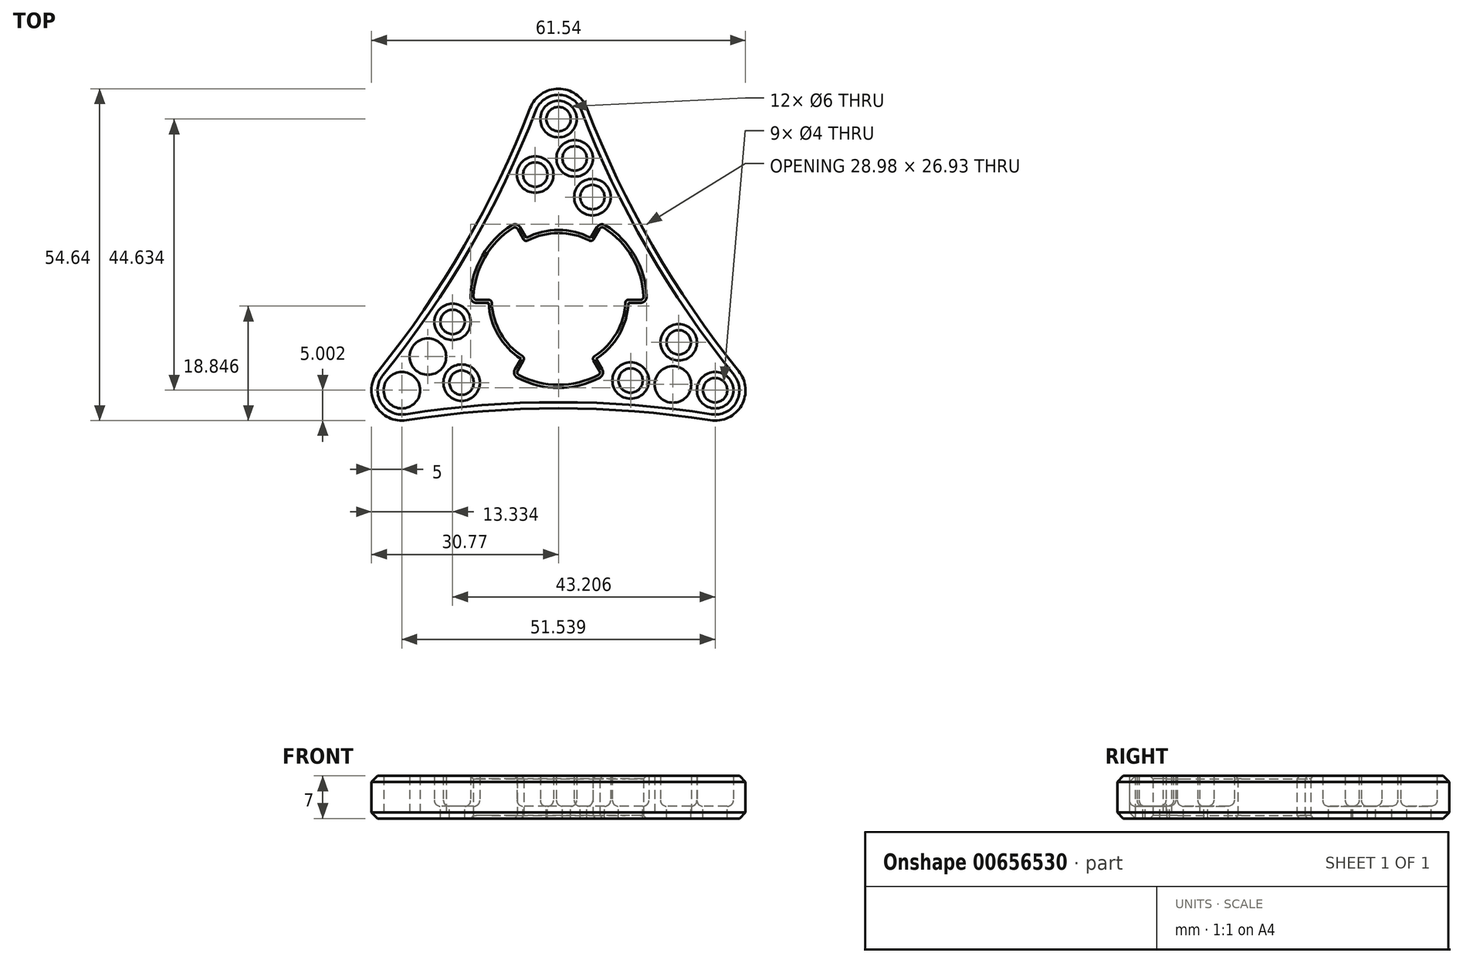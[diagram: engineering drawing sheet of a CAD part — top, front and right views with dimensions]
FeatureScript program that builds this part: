
annotation { "Feature Type Name" : "Feature", "Feature Type Description" : "" }
export const myFeature = defineFeature(function(context is Context, id is Id, definition is map)
    precondition{}
    {
        {
            var Q0;
            Q0=qCreatedBy(makeId("Top.planeOp"),FACE);
            var sketch = newSketch(context, id + "F0", { "sketchPlane" : qUnion([Q0])});
            skCircle(sketch, "E0", {"center": v(0, 0) * mm, "radius": 11 * mm});
            skCircle(sketch, "E1", {"center": v(0, 29.76) * mm, "radius": 3 * mm});
            skCircle(sketch, "E2", {"center": v(-3.83, 20.63) * mm, "radius": 3 * mm});
            skCircle(sketch, "E3", {"center": v(2.65, 23.28) * mm, "radius": 3 * mm});
            skLineSegment(sketch, "E4", {"start": v(0, 0) * mm, "end": v(0, 29.76) * mm, "construction": true});
            skLineSegment(sketch, "E5", {"start": v(0, 45.58) * mm, "end": v(39.48, -22.8) * mm, "construction": true});
            skLineSegment(sketch, "E6", {"start": v(39.48, -22.8) * mm, "end": v(-39.48, -22.8) * mm, "construction": true});
            skLineSegment(sketch, "E7", {"start": v(-39.48, -22.8) * mm, "end": v(0, 45.58) * mm, "construction": true});
            skLineSegment(sketch, "E8", {"start": v(0, 0) * mm, "end": v(-39.48, -22.8) * mm, "construction": true});
            skCircle(sketch, "E9", {"center": v(0, 0) * mm, "radius": 14 * mm});
            skLineSegment(sketch, "E10", {"start": v(-7, 12.12) * mm, "end": v(-5.5, 9.53) * mm});
            skLineSegment(sketch, "E11", {"start": v(-14, 0) * mm, "end": v(-11, 0) * mm});
            skArc(sketch, "E12", {"start": v(0, 45.58) * mm, "mid": v(15.47, 8.93) * mm, "end": v(39.48, -22.8) * mm});
            skArc(sketch, "E13", {"start": v(-39.48, -22.8) * mm, "mid": v(-15.47, 8.93) * mm, "end": v(0, 45.58) * mm});
            skArc(sketch, "E14", {"start": v(39.48, -22.8) * mm, "mid": v(0, -17.86) * mm, "end": v(-39.48, -22.8) * mm});
            skCircle(sketch, "E15", {"center": v(5.57, 16.92) * mm, "radius": 3 * mm});
            skLineSegment(sketch, "E16", {"start": v(-3.83, 20.63) * mm, "end": v(2.65, 23.28) * mm, "construction": true});
            skLineSegment(sketch, "E17", {"start": v(0, 29.76) * mm, "end": v(2.65, 23.28) * mm, "construction": true});
            skCircle(sketch, "E18.1.0", {"center": v(-25.77, -14.88) * mm, "radius": 3 * mm});
            skCircle(sketch, "E18.1.1", {"center": v(-21.48, -9.34) * mm, "radius": 3 * mm});
            skCircle(sketch, "E18.1.2", {"center": v(-17.44, -3.63) * mm, "radius": 3 * mm});
            skCircle(sketch, "E18.1.3", {"center": v(-15.95, -13.63) * mm, "radius": 3 * mm});
            skLineSegment(sketch, "E18.1.4", {"start": v(-7, -12.12) * mm, "end": v(-5.5, -9.53) * mm});
            skLineSegment(sketch, "E18.1.5", {"start": v(7, -12.12) * mm, "end": v(5.5, -9.53) * mm});
            skCircle(sketch, "E18.2.0", {"center": v(25.77, -14.88) * mm, "radius": 3 * mm});
            skCircle(sketch, "E18.2.1", {"center": v(18.83, -13.93) * mm, "radius": 3 * mm});
            skCircle(sketch, "E18.2.2", {"center": v(11.86, -13.28) * mm, "radius": 3 * mm});
            skCircle(sketch, "E18.2.3", {"center": v(19.78, -7) * mm, "radius": 3 * mm});
            skLineSegment(sketch, "E18.2.4", {"start": v(14, 0) * mm, "end": v(11, 0) * mm});
            skLineSegment(sketch, "E18.2.5", {"start": v(7, 12.12) * mm, "end": v(5.5, 9.53) * mm});
            skSolve(sketch);
        }
        {
            var Q0;
            Q0=makeQuery(id+"F0.imprint","IMPRINT",FACE,{"disambiguationData":[TD([[makeQuery(id+"F0.imprint","IMPRINT",EDGE,{"derivedFrom":sQuery(id+"F0.wireOp",EDGE,"E1")}),-1.0]])]});
            var Q1;
            {var subQ0=sQuery(id+"F0.wireOp",EDGE,"E10");Q1=makeQuery(id+"F0.imprint","IMPRINT",FACE,{"disambiguationData":[TD([[makeQuery(id+"F0.imprint","IMPRINT",EDGE,{"derivedFrom":subQ0}),1.0]])]});}
            var Q2;
            {var subQ0=sQuery(id+"F0.wireOp",EDGE,"E11");Q2=makeQuery(id+"F0.imprint","IMPRINT",FACE,{"disambiguationData":[TD([[makeQuery(id+"F0.imprint","IMPRINT",EDGE,{"derivedFrom":subQ0}),-1.0]])]});}
            var Q3;
            {var subQ0=sQuery(id+"F0.wireOp",EDGE,"f7c1c19d-2732-4989-aeff-ee9fb130af58.1.6");Q3=makeQuery(id+"F0.imprint","IMPRINT",FACE,{"disambiguationData":[TD([[makeQuery(id+"F0.imprint","IMPRINT",EDGE,{"derivedFrom":subQ0}),-1.0]])]});}
            var Q4;
            {var subQ0=sQuery(id+"F0.wireOp",EDGE,"E18.1.5");Q4=makeQuery(id+"F0.imprint","IMPRINT",FACE,{"disambiguationData":[TD([[makeQuery(id+"F0.imprint","IMPRINT",EDGE,{"derivedFrom":subQ0}),-1.0]])]});}
            extrude(context, id + "F1", {"entities" : qUnion([Q0, Q1, Q2, Q3, Q4]), "depth" : 7 * mm, "offsetDistance" : 25 * mm});
        }
        {
            var Q0;
            Q0=makeQuery(id+"F1.opExtrude","SWEPT_EDGE",EDGE,{"disambiguationData":[OSD([sQuery(id+"F0.wireOp",EDGE,"E12"),sQuery(id+"F0.wireOp",EDGE,"E14")])]});
            var Q1;
            Q1=makeQuery(id+"F1.opExtrude","SWEPT_EDGE",EDGE,{"disambiguationData":[OSD([sQuery(id+"F0.wireOp",EDGE,"E13"),sQuery(id+"F0.wireOp",EDGE,"E14")])]});
            var Q2;
            Q2=makeQuery(id+"F1.opExtrude","SWEPT_EDGE",EDGE,{"disambiguationData":[OSD([sQuery(id+"F0.wireOp",EDGE,"E12"),sQuery(id+"F0.wireOp",EDGE,"E13")])]});
            fillet(context, id + "F2", {"entities" : qUnion([Q0, Q1, Q2]), "radius" : 5 * mm, "tangentPropagation" : true, "allowEdgeOverflow" : false});
        }
        {
            var Q0;
            Q0=makeQuery(id+"F1.opExtrude","SWEPT_EDGE",EDGE,{"disambiguationData":[OSD([sQuery(id+"F0.wireOp",EDGE,"E9"),sQuery(id+"F0.wireOp",EDGE,"E10")])]});
            var Q1;
            Q1=makeQuery(id+"F1.opExtrude","SWEPT_EDGE",EDGE,{"disambiguationData":[OSD([sQuery(id+"F0.wireOp",EDGE,"E0"),sQuery(id+"F0.wireOp",EDGE,"E10")])]});
            var Q2;
            Q2=makeQuery(id+"F1.opExtrude","SWEPT_EDGE",EDGE,{"disambiguationData":[OSD([sQuery(id+"F0.wireOp",EDGE,"E0"),sQuery(id+"F0.wireOp",EDGE,"E18.2.5")])]});
            var Q3;
            Q3=makeQuery(id+"F1.opExtrude","SWEPT_EDGE",EDGE,{"disambiguationData":[OSD([sQuery(id+"F0.wireOp",EDGE,"E9"),sQuery(id+"F0.wireOp",EDGE,"E18.2.5")])]});
            var Q4;
            Q4=makeQuery(id+"F1.opExtrude","SWEPT_EDGE",EDGE,{"disambiguationData":[OSD([sQuery(id+"F0.wireOp",EDGE,"E9"),sQuery(id+"F0.wireOp",EDGE,"E18.2.4")])]});
            var Q5;
            Q5=makeQuery(id+"F1.opExtrude","SWEPT_EDGE",EDGE,{"disambiguationData":[OSD([sQuery(id+"F0.wireOp",EDGE,"E0"),sQuery(id+"F0.wireOp",EDGE,"E18.2.4")])]});
            var Q6;
            Q6=makeQuery(id+"F1.opExtrude","SWEPT_EDGE",EDGE,{"disambiguationData":[OSD([sQuery(id+"F0.wireOp",EDGE,"E0"),sQuery(id+"F0.wireOp",EDGE,"E18.1.5")])]});
            var Q7;
            Q7=makeQuery(id+"F1.opExtrude","SWEPT_EDGE",EDGE,{"disambiguationData":[OSD([sQuery(id+"F0.wireOp",EDGE,"E9"),sQuery(id+"F0.wireOp",EDGE,"E18.1.5")])]});
            var Q8;
            Q8=makeQuery(id+"F1.opExtrude","SWEPT_EDGE",EDGE,{"disambiguationData":[OSD([sQuery(id+"F0.wireOp",EDGE,"E9"),sQuery(id+"F0.wireOp",EDGE,"E11")])]});
            var Q9;
            Q9=makeQuery(id+"F1.opExtrude","SWEPT_EDGE",EDGE,{"disambiguationData":[OSD([sQuery(id+"F0.wireOp",EDGE,"E0"),sQuery(id+"F0.wireOp",EDGE,"E11")])]});
            var Q10;
            Q10=makeQuery(id+"F1.opExtrude","SWEPT_EDGE",EDGE,{"disambiguationData":[OSD([sQuery(id+"F0.wireOp",EDGE,"E9"),sQuery(id+"F0.wireOp",EDGE,"E18.1.4")])]});
            var Q11;
            Q11=makeQuery(id+"F1.opExtrude","SWEPT_EDGE",EDGE,{"disambiguationData":[OSD([sQuery(id+"F0.wireOp",EDGE,"E0"),sQuery(id+"F0.wireOp",EDGE,"E18.1.4")])]});
            fillet(context, id + "F3", {"entities" : qUnion([Q0, Q1, Q2, Q3, Q4, Q5, Q6, Q7, Q8, Q9, Q10, Q11]), "radius" : 0.5 * mm, "tangentPropagation" : true, "allowEdgeOverflow" : false});
        }
        {
            var Q0;
            {var subQ0=sQuery(id+"F0.wireOp",EDGE,"E0");Q0=makeQuery(id+"F1.opExtrude","CAP_EDGE",EDGE,{"disambiguationData":[OSD([subQ0]),TDD([makeQuery(id+"F0.imprint","IMPRINT",EDGE,{"disambiguationData":[TD([[makeQuery(id+"F0.imprint","INTERSECT",VERTEX,{"derivedFrom":[subQ0,sQuery(id+"F0.wireOp",EDGE,"E18.1.5")]}),-1.0]])],"derivedFrom":subQ0})])],"isStart":true});}
            var Q1;
            {var subQ0=sQuery(id+"F0.wireOp",EDGE,"E0");Q1=makeQuery(id+"F1.opExtrude","CAP_EDGE",EDGE,{"disambiguationData":[OSD([subQ0]),TDD([makeQuery(id+"F0.imprint","IMPRINT",EDGE,{"disambiguationData":[TD([[makeQuery(id+"F0.imprint","INTERSECT",VERTEX,{"derivedFrom":[subQ0,sQuery(id+"F0.wireOp",EDGE,"E18.1.5")]}),-1.0]])],"derivedFrom":subQ0})])],"isStart":false});}
            chamfer(context, id + "F4", {"entities" : qUnion([Q0, Q1]), "width" : 0.5 * mm, "tangentPropagation" : true});
        }
        {
            var Q0;
            Q0=makeQuery(id+"F0.imprint","IMPRINT",FACE,{"disambiguationData":[TD([[makeQuery(id+"F0.imprint","IMPRINT",EDGE,{"derivedFrom":sQuery(id+"F0.wireOp",EDGE,"E1")}),1.0]])]});
            var Q1;
            Q1=makeQuery(id+"F0.imprint","IMPRINT",FACE,{"disambiguationData":[TD([[makeQuery(id+"F0.imprint","IMPRINT",EDGE,{"derivedFrom":sQuery(id+"F0.wireOp",EDGE,"E3")}),1.0]])]});
            var Q2;
            Q2=makeQuery(id+"F0.imprint","IMPRINT",FACE,{"disambiguationData":[TD([[makeQuery(id+"F0.imprint","IMPRINT",EDGE,{"derivedFrom":sQuery(id+"F0.wireOp",EDGE,"E15")}),1.0]])]});
            var Q3;
            Q3=makeQuery(id+"F0.imprint","IMPRINT",FACE,{"disambiguationData":[TD([[makeQuery(id+"F0.imprint","IMPRINT",EDGE,{"derivedFrom":sQuery(id+"F0.wireOp",EDGE,"E2")}),1.0]])]});
            var Q4;
            Q4=makeQuery(id+"F0.imprint","IMPRINT",FACE,{"disambiguationData":[TD([[makeQuery(id+"F0.imprint","IMPRINT",EDGE,{"derivedFrom":sQuery(id+"F0.wireOp",EDGE,"E18.1.2")}),1.0]])]});
            var Q5;
            Q5=makeQuery(id+"F0.imprint","IMPRINT",FACE,{"disambiguationData":[TD([[makeQuery(id+"F0.imprint","IMPRINT",EDGE,{"derivedFrom":sQuery(id+"F0.wireOp",EDGE,"E18.1.1")}),1.0]])]});
            var Q6;
            Q6=makeQuery(id+"F0.imprint","IMPRINT",FACE,{"disambiguationData":[TD([[makeQuery(id+"F0.imprint","IMPRINT",EDGE,{"derivedFrom":sQuery(id+"F0.wireOp",EDGE,"E18.1.0")}),1.0]])]});
            var Q7;
            Q7=makeQuery(id+"F0.imprint","IMPRINT",FACE,{"disambiguationData":[TD([[makeQuery(id+"F0.imprint","IMPRINT",EDGE,{"derivedFrom":sQuery(id+"F0.wireOp",EDGE,"E18.1.3")}),1.0]])]});
            var Q8;
            Q8=makeQuery(id+"F0.imprint","IMPRINT",FACE,{"disambiguationData":[TD([[makeQuery(id+"F0.imprint","IMPRINT",EDGE,{"derivedFrom":sQuery(id+"F0.wireOp",EDGE,"E18.2.2")}),1.0]])]});
            var Q9;
            Q9=makeQuery(id+"F0.imprint","IMPRINT",FACE,{"disambiguationData":[TD([[makeQuery(id+"F0.imprint","IMPRINT",EDGE,{"derivedFrom":sQuery(id+"F0.wireOp",EDGE,"E18.2.1")}),1.0]])]});
            var Q10;
            Q10=makeQuery(id+"F0.imprint","IMPRINT",FACE,{"disambiguationData":[TD([[makeQuery(id+"F0.imprint","IMPRINT",EDGE,{"derivedFrom":sQuery(id+"F0.wireOp",EDGE,"E18.2.0")}),1.0]])]});
            var Q11;
            Q11=makeQuery(id+"F0.imprint","IMPRINT",FACE,{"disambiguationData":[TD([[makeQuery(id+"F0.imprint","IMPRINT",EDGE,{"derivedFrom":sQuery(id+"F0.wireOp",EDGE,"E18.2.3")}),1.0]])]});
            extrude(context, id + "F5", {"entities" : qUnion([Q0, Q1, Q2, Q3, Q4, Q5, Q6, Q7, Q8, Q9, Q10, Q11]), "operationType" : NewBodyOperationType.ADD, "depth" : 2 * mm, "offsetDistance" : 25 * mm});
        }
        {
            var Q0;
            Q0=makeQuery(id+"F1.opExtrude","CAP_EDGE",EDGE,{"disambiguationData":[OSD([sQuery(id+"F0.wireOp",EDGE,"E14")])],"isStart":true});
            var Q1;
            Q1=makeQuery(id+"F1.opExtrude","CAP_EDGE",EDGE,{"disambiguationData":[OSD([sQuery(id+"F0.wireOp",EDGE,"E14")])],"isStart":false});
            chamfer(context, id + "F6", {"entities" : qUnion([Q0, Q1]), "width" : 1 * mm, "tangentPropagation" : true});
        }
        {
            var Q0;
            Q0=makeQuery(id+"F5.opExtrude","CAP_EDGE",EDGE,{"disambiguationData":[OSD([sQuery(id+"F0.wireOp",EDGE,"E18.1.0")])],"isStart":false});
            var Q1;
            Q1=makeQuery(id+"F5.opExtrude","CAP_EDGE",EDGE,{"disambiguationData":[OSD([sQuery(id+"F0.wireOp",EDGE,"E18.1.1")])],"isStart":false});
            var Q2;
            Q2=makeQuery(id+"F5.opExtrude","CAP_FACE",FACE,{"disambiguationData":[OSD([sQuery(id+"F0.wireOp",EDGE,"E18.1.2")])],"isStart":false});
            var Q3;
            Q3=makeQuery(id+"F5.opExtrude","CAP_FACE",FACE,{"disambiguationData":[OSD([sQuery(id+"F0.wireOp",EDGE,"E18.1.3")])],"isStart":false});
            var Q4;
            Q4=makeQuery(id+"F5.opExtrude","CAP_FACE",FACE,{"disambiguationData":[OSD([sQuery(id+"F0.wireOp",EDGE,"E2")])],"isStart":false});
            var Q5;
            Q5=makeQuery(id+"F5.opExtrude","CAP_FACE",FACE,{"disambiguationData":[OSD([sQuery(id+"F0.wireOp",EDGE,"E1")])],"isStart":false});
            var Q6;
            Q6=makeQuery(id+"F5.opExtrude","CAP_FACE",FACE,{"disambiguationData":[OSD([sQuery(id+"F0.wireOp",EDGE,"E3")])],"isStart":false});
            var Q7;
            Q7=makeQuery(id+"F5.opExtrude","CAP_FACE",FACE,{"disambiguationData":[OSD([sQuery(id+"F0.wireOp",EDGE,"E15")])],"isStart":false});
            var Q8;
            Q8=makeQuery(id+"F5.opExtrude","CAP_FACE",FACE,{"disambiguationData":[OSD([sQuery(id+"F0.wireOp",EDGE,"E18.2.3")])],"isStart":false});
            var Q9;
            Q9=makeQuery(id+"F5.opExtrude","CAP_FACE",FACE,{"disambiguationData":[OSD([sQuery(id+"F0.wireOp",EDGE,"E18.2.2")])],"isStart":false});
            var Q10;
            Q10=makeQuery(id+"F5.opExtrude","CAP_EDGE",EDGE,{"disambiguationData":[OSD([sQuery(id+"F0.wireOp",EDGE,"E18.2.1")])],"isStart":false});
            var Q11;
            Q11=makeQuery(id+"F5.opExtrude","CAP_FACE",FACE,{"disambiguationData":[OSD([sQuery(id+"F0.wireOp",EDGE,"E18.2.0")])],"isStart":false});
            fillet(context, id + "F7", {"entities" : qUnion([Q0, Q1, Q2, Q3, Q4, Q5, Q6, Q7, Q8, Q9, Q10, Q11]), "radius" : 1 * mm, "tangentPropagation" : true, "allowEdgeOverflow" : false});
        }
        {
            var Q0;
            Q0=makeQuery(id+"F5.opExtrude","CAP_FACE",FACE,{"disambiguationData":[OSD([sQuery(id+"F0.wireOp",EDGE,"E18.2.0")])],"isStart":false});
            var Q1;
            Q1=makeQuery(id+"F5.opExtrude","CAP_FACE",FACE,{"disambiguationData":[OSD([sQuery(id+"F0.wireOp",EDGE,"E18.2.1")])],"isStart":false});
            var Q2;
            Q2=makeQuery(id+"F5.opExtrude","CAP_FACE",FACE,{"disambiguationData":[OSD([sQuery(id+"F0.wireOp",EDGE,"E18.2.3")])],"isStart":false});
            var Q3;
            Q3=makeQuery(id+"F5.opExtrude","CAP_FACE",FACE,{"disambiguationData":[OSD([sQuery(id+"F0.wireOp",EDGE,"E18.2.2")])],"isStart":false});
            var Q4;
            Q4=makeQuery(id+"F5.opExtrude","CAP_FACE",FACE,{"disambiguationData":[OSD([sQuery(id+"F0.wireOp",EDGE,"E15")])],"isStart":false});
            var Q5;
            Q5=makeQuery(id+"F5.opExtrude","CAP_FACE",FACE,{"disambiguationData":[OSD([sQuery(id+"F0.wireOp",EDGE,"E3")])],"isStart":false});
            var Q6;
            Q6=makeQuery(id+"F5.opExtrude","CAP_FACE",FACE,{"disambiguationData":[OSD([sQuery(id+"F0.wireOp",EDGE,"E1")])],"isStart":false});
            var Q7;
            Q7=makeQuery(id+"F5.opExtrude","CAP_FACE",FACE,{"disambiguationData":[OSD([sQuery(id+"F0.wireOp",EDGE,"E2")])],"isStart":false});
            var Q8;
            Q8=makeQuery(id+"F5.opExtrude","CAP_FACE",FACE,{"disambiguationData":[OSD([sQuery(id+"F0.wireOp",EDGE,"E18.1.2")])],"isStart":false});
            var Q9;
            Q9=makeQuery(id+"F5.opExtrude","CAP_FACE",FACE,{"disambiguationData":[OSD([sQuery(id+"F0.wireOp",EDGE,"E18.1.1")])],"isStart":false});
            var Q10;
            Q10=makeQuery(id+"F5.opExtrude","CAP_FACE",FACE,{"disambiguationData":[OSD([sQuery(id+"F0.wireOp",EDGE,"E18.1.0")])],"isStart":false});
            var Q11;
            Q11=makeQuery(id+"F5.opExtrude","CAP_FACE",FACE,{"disambiguationData":[OSD([sQuery(id+"F0.wireOp",EDGE,"E18.1.3")])],"isStart":false});
            extrude(context, id + "F8", {"entities" : qUnion([Q0, Q1, Q2, Q3, Q4, Q5, Q6, Q7, Q8, Q9, Q10, Q11]), "operationType" : NewBodyOperationType.REMOVE, "oppositeDirection" : true, "depth" : 25 * mm, "offsetDistance" : 25 * mm});
        }
    });
